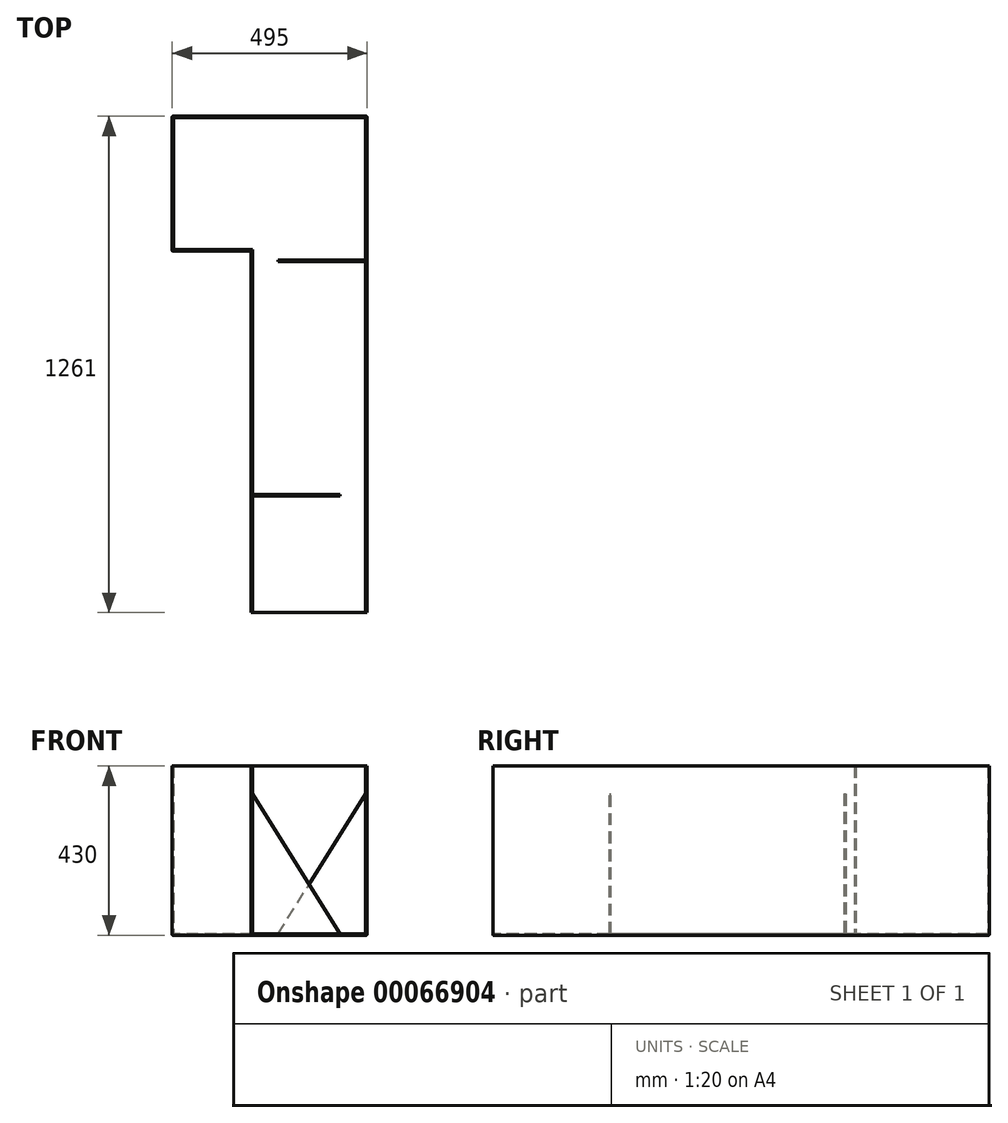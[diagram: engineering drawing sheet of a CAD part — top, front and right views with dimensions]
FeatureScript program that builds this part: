
annotation { "Feature Type Name" : "Feature", "Feature Type Description" : "" }
export const myFeature = defineFeature(function(context is Context, id is Id, definition is map)
    precondition{}
    {
        {
            var Q0;
            Q0=qCreatedBy(makeId("Top.planeOp"),FACE);
            var sketch = newSketch(context, id + "F0", { "sketchPlane" : qUnion([Q0])});
            skLineSegment(sketch, "E0", {"start": v(0, 0) * mm, "end": v(495, 0) * mm});
            skLineSegment(sketch, "E1", {"start": v(200, -343) * mm, "end": v(0, -343) * mm});
            skLineSegment(sketch, "E2", {"start": v(0, -343) * mm, "end": v(0, 0) * mm});
            skLineSegment(sketch, "E3.right", {"start": v(200, -343) * mm, "end": v(200, -1261) * mm});
            skLineSegment(sketch, "E4.left", {"start": v(495, 0) * mm, "end": v(495, -1261) * mm});
            skLineSegment(sketch, "E5.0", {"start": v(491, -4) * mm, "end": v(491, -1261) * mm});
            skLineSegment(sketch, "E5.1", {"start": v(204, -339) * mm, "end": v(204, -1261) * mm});
            skLineSegment(sketch, "E5.2", {"start": v(204, -339) * mm, "end": v(4, -339) * mm});
            skLineSegment(sketch, "E5.3", {"start": v(4, -339) * mm, "end": v(4, -4) * mm});
            skLineSegment(sketch, "E5.4", {"start": v(4, -4) * mm, "end": v(491, -4) * mm});
            skLineSegment(sketch, "E6", {"start": v(204, -1261) * mm, "end": v(200, -1261) * mm});
            skLineSegment(sketch, "E7", {"start": v(491, -1261) * mm, "end": v(495, -1261) * mm});
            skSolve(sketch);
        }
        {
            var Q0;
            Q0=makeQuery(id+"F0.imprint","IMPRINT",FACE,{"disambiguationData":[TD([[makeQuery(id+"F0.imprint","IMPRINT",EDGE,{"derivedFrom":sQuery(id+"F0.wireOp",EDGE,"E0")}),-1.0]])]});
            extrude(context, id + "F1", {"entities" : qUnion([Q0]), "depth" : 426 * mm});
        }
        {
            var Q0;
            Q0=qCreatedBy(makeId("Top.planeOp"),FACE);
            var sketch = newSketch(context, id + "F2", { "sketchPlane" : qUnion([Q0])});
            skLineSegment(sketch, "E8.0", {"start": v(200, -343) * mm, "end": v(0, -343) * mm});
            skLineSegment(sketch, "E9.0", {"start": v(0, -343) * mm, "end": v(0, 0) * mm});
            skLineSegment(sketch, "E10.0", {"start": v(0, 0) * mm, "end": v(0, 0) * mm});
            skLineSegment(sketch, "E11.0", {"start": v(0, 0) * mm, "end": v(495, 0) * mm});
            skLineSegment(sketch, "E12.0", {"start": v(200, -343) * mm, "end": v(200, -343) * mm});
            skLineSegment(sketch, "E13.0", {"start": v(495, 0) * mm, "end": v(495, 0) * mm});
            skLineSegment(sketch, "E14.0", {"start": v(495, 0) * mm, "end": v(495, -1261) * mm});
            skLineSegment(sketch, "E15", {"start": v(495, -1261) * mm, "end": v(200, -1261) * mm});
            skLineSegment(sketch, "E16", {"start": v(200, -1261) * mm, "end": v(200, -343) * mm});
            skSolve(sketch);
        }
        {
            var Q0;
            Q0=qSketchRegion(id+"F2",true);
            extrude(context, id + "F3", {"entities" : qUnion([Q0]), "operationType" : NewBodyOperationType.ADD, "oppositeDirection" : true, "depth" : 4 * mm});
        }
        {
            var Q0;
            Q0=makeQuery(id+"F3.opExtrude","CAP_EDGE",EDGE,{"disambiguationData":[OSD([sQuery(id+"F2.wireOp",EDGE,"E13.0")])],"isStart":false});
            var Q1;
            Q1=makeQuery(id+"F3.opExtrude","CAP_EDGE",EDGE,{"disambiguationData":[OSD([sQuery(id+"F2.wireOp",EDGE,"E8.0")])],"isStart":false});
            var Q2;
            Q2=makeQuery(id+"F3.opExtrude","CAP_EDGE",EDGE,{"disambiguationData":[OSD([sQuery(id+"F2.wireOp",EDGE,"E12.0")])],"isStart":false});
            var Q3;
            Q3=makeQuery(id+"F3.opExtrude","CAP_EDGE",EDGE,{"disambiguationData":[OSD([sQuery(id+"F2.wireOp",EDGE,"E9.0")])],"isStart":false});
            var Q4;
            Q4=makeQuery(id+"F3.opExtrude","CAP_EDGE",EDGE,{"disambiguationData":[OSD([sQuery(id+"F2.wireOp",EDGE,"E11.0")])],"isStart":false});
            var Q5;
            Q5=makeQuery(id+"F3.boolean.opBoolean","MERGE",EDGE,{"derivedFrom":[makeQuery(id+"F1.opExtrude","SWEPT_EDGE",EDGE,{"disambiguationData":[OSD([sQuery(id+"F0.wireOp",EDGE,"E1"),sQuery(id+"F0.wireOp",EDGE,"E3.right")])]}),makeQuery(id+"F3.opExtrude","SWEPT_EDGE",EDGE,{"disambiguationData":[OSD([sQuery(id+"F2.wireOp",EDGE,"E8.0"),sQuery(id+"F2.wireOp",EDGE,"E12.0")])]})]});
            var Q6;
            Q6=makeQuery(id+"F3.boolean.opBoolean","MERGE",EDGE,{"derivedFrom":[makeQuery(id+"F1.opExtrude","SWEPT_EDGE",EDGE,{"disambiguationData":[OSD([sQuery(id+"F0.wireOp",EDGE,"E1"),sQuery(id+"F0.wireOp",EDGE,"E2")])]}),makeQuery(id+"F3.opExtrude","SWEPT_EDGE",EDGE,{"disambiguationData":[OSD([sQuery(id+"F2.wireOp",EDGE,"E8.0"),sQuery(id+"F2.wireOp",EDGE,"E9.0")])]})]});
            var Q7;
            Q7=makeQuery(id+"F3.boolean.opBoolean","MERGE",EDGE,{"derivedFrom":[makeQuery(id+"F1.opExtrude","SWEPT_EDGE",EDGE,{"disambiguationData":[OSD([sQuery(id+"F0.wireOp",EDGE,"E0"),sQuery(id+"F0.wireOp",EDGE,"E2")])]}),makeQuery(id+"F3.opExtrude","SWEPT_EDGE",EDGE,{"disambiguationData":[OSD([sQuery(id+"F2.wireOp",EDGE,"E9.0"),sQuery(id+"F2.wireOp",EDGE,"E11.0")])]})]});
            var Q8;
            Q8=makeQuery(id+"F1.opExtrude","SWEPT_EDGE",EDGE,{"disambiguationData":[OSD([sQuery(id+"F0.wireOp",EDGE,"41269a5a-69f6-4670-b1a7-19bf830e781a"),sQuery(id+"F0.wireOp",EDGE,"E4.right")])]});
            var Q9;
            Q9=makeQuery(id+"F1.opExtrude","SWEPT_EDGE",EDGE,{"disambiguationData":[OSD([sQuery(id+"F0.wireOp",EDGE,"cc5772d9-c29a-4c81-bde5-837d5d9decb7"),sQuery(id+"F0.wireOp",EDGE,"E3.left")])]});
            var Q10;
            Q10=makeQuery(id+"F1.opExtrude","SWEPT_EDGE",EDGE,{"disambiguationData":[OSD([sQuery(id+"F0.wireOp",EDGE,"41269a5a-69f6-4670-b1a7-19bf830e781a"),sQuery(id+"F0.wireOp",EDGE,"05cfef9b-c223-4bdb-b400-77ea615546ad")])]});
            var Q11;
            Q11=makeQuery(id+"F1.opExtrude","SWEPT_EDGE",EDGE,{"disambiguationData":[OSD([sQuery(id+"F0.wireOp",EDGE,"05cfef9b-c223-4bdb-b400-77ea615546ad"),sQuery(id+"F0.wireOp",EDGE,"cc5772d9-c29a-4c81-bde5-837d5d9decb7")])]});
            var Q12;
            Q12=makeQuery(id+"F3.boolean.opBoolean","MERGE",EDGE,{"derivedFrom":[makeQuery(id+"F1.opExtrude","SWEPT_EDGE",EDGE,{"disambiguationData":[OSD([sQuery(id+"F0.wireOp",EDGE,"E0"),sQuery(id+"F0.wireOp",EDGE,"E4.left")])]}),makeQuery(id+"F3.opExtrude","SWEPT_EDGE",EDGE,{"disambiguationData":[OSD([sQuery(id+"F2.wireOp",EDGE,"E11.0"),sQuery(id+"F2.wireOp",EDGE,"E13.0")])]})]});
            var Q13;
            Q13=makeQuery(id+"F3.opExtrude","CAP_EDGE",EDGE,{"disambiguationData":[OSD([sQuery(id+"F2.wireOp",EDGE,"E16")])],"isStart":false});
            var Q14;
            Q14=makeQuery(id+"F3.opExtrude","CAP_EDGE",EDGE,{"disambiguationData":[OSD([sQuery(id+"F2.wireOp",EDGE,"E14.0")])],"isStart":false});
            fillet(context, id + "F4", {"entities" : qUnion([Q0, Q1, Q2, Q3, Q4, Q5, Q6, Q7, Q8, Q9, Q10, Q11, Q12, Q13, Q14]), "radius" : 2 * mm, "tangentPropagation" : true, "allowEdgeOverflow" : false});
        }
        {
            var Q0;
            Q0=makeQuery(id+"F3.boolean.opBoolean","MERGE",FACE,{"derivedFrom":[makeQuery(id+"F1.opExtrude","SWEPT_FACE",FACE,{"disambiguationData":[OSD([sQuery(id+"F0.wireOp",EDGE,"E6")])]}),makeQuery(id+"F1.opExtrude","SWEPT_FACE",FACE,{"disambiguationData":[OSD([sQuery(id+"F0.wireOp",EDGE,"E7")])]}),makeQuery(id+"F3.opExtrude","SWEPT_FACE",FACE,{"disambiguationData":[OSD([sQuery(id+"F2.wireOp",EDGE,"E15")])]})]});
            cPlane(context, id + "F5", {"entities" : qUnion([Q0]), "cplaneType" : CPlaneType.OFFSET, "offset" : 300 * mm, "oppositeDirection" : true, "width" : 150 * mm, "height" : 150 * mm});
        }
        {
            var Q0;
            Q0=qCreatedBy(id+"F5.planeOp",FACE);
            var sketch = newSketch(context, id + "F6", { "sketchPlane" : qUnion([Q0])});
            skLineSegment(sketch, "E17", {"start": v(204, 0) * mm, "end": v(204, 355) * mm});
            skLineSegment(sketch, "E18", {"start": v(204, 355) * mm, "end": v(426, 0) * mm});
            skLineSegment(sketch, "E19", {"start": v(426, 0) * mm, "end": v(204, 0) * mm});
            skSolve(sketch);
        }
        {
            var Q0;
            Q0=makeQuery(id+"F6.imprint","IMPRINT",FACE,{"disambiguationData":[TD([[makeQuery(id+"F6.imprint","IMPRINT",EDGE,{"derivedFrom":sQuery(id+"F6.wireOp",EDGE,"E17")}),-1.0]])]});
            extrude(context, id + "F7", {"entities" : qUnion([Q0]), "operationType" : NewBodyOperationType.ADD, "depth" : 4 * mm});
        }
        {
            var Q0;
            Q0=makeQuery(id+"F7.opExtrude","CAP_FACE",FACE,{"disambiguationData":[OSD([sQuery(id+"F6.wireOp",EDGE,"E17"),sQuery(id+"F6.wireOp",EDGE,"E18"),sQuery(id+"F6.wireOp",EDGE,"E19")])],"isStart":false});
            cPlane(context, id + "F8", {"entities" : qUnion([Q0]), "cplaneType" : CPlaneType.OFFSET, "offset" : 600 * mm, "oppositeDirection" : true, "width" : 150 * mm, "height" : 150 * mm});
        }
        {
            var Q0;
            Q0=qCreatedBy(id+"F8.planeOp",FACE);
            var sketch = newSketch(context, id + "F9", { "sketchPlane" : qUnion([Q0])});
            skLineSegment(sketch, "E20", {"start": v(491, 0) * mm, "end": v(269, 0) * mm});
            skLineSegment(sketch, "E21", {"start": v(269, 0) * mm, "end": v(491, 355) * mm});
            skLineSegment(sketch, "E22", {"start": v(491, 355) * mm, "end": v(491, 0) * mm});
            skSolve(sketch);
        }
        {
            var Q0;
            Q0 = qSketchRegion(id + "F9", true);
            extrude(context, id + "F10", {"entities" : qUnion([Q0]), "operationType" : NewBodyOperationType.ADD, "depth" : 4 * mm});
        }
    });
